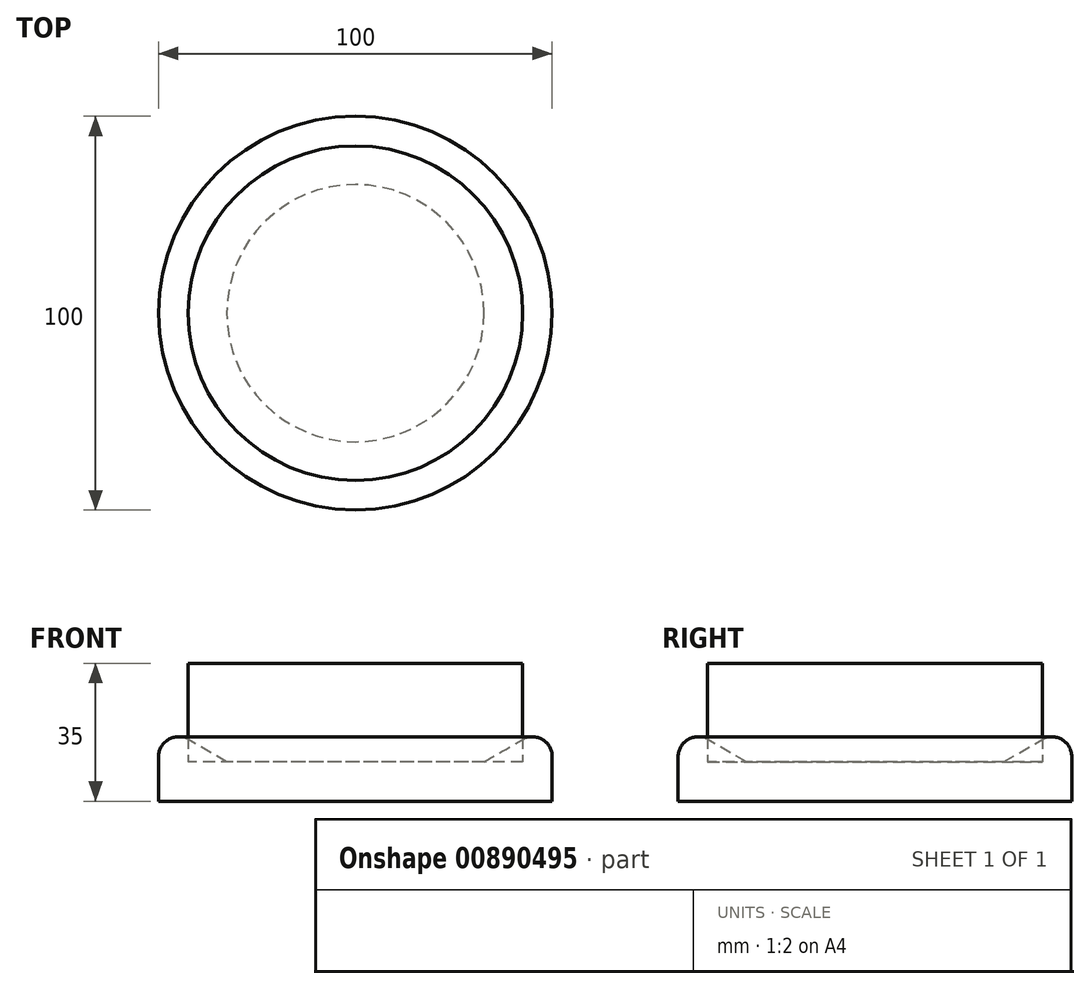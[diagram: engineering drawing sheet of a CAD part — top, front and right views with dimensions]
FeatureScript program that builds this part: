
annotation { "Feature Type Name" : "Feature", "Feature Type Description" : "" }
export const myFeature = defineFeature(function(context is Context, id is Id, definition is map)
    precondition{}
    {
        {
            var Q0;
            Q0=qCreatedBy(makeId("Front.planeOp"),FACE);
            var sketch = newSketch(context, id + "F0", { "sketchPlane" : qUnion([Q0])});
            skLineSegment(sketch, "E0", {"start": v(0, 0) * mm, "end": v(-50, 0) * mm});
            skLineSegment(sketch, "E1", {"start": v(-50, 0) * mm, "end": v(-50, 20) * mm});
            skLineSegment(sketch, "E2", {"start": v(-50, 20) * mm, "end": v(-32.68, 10) * mm});
            skLineSegment(sketch, "E3", {"start": v(-32.68, 10) * mm, "end": v(0, 10) * mm});
            skLineSegment(sketch, "E4", {"start": v(0, 10) * mm, "end": v(0, 0) * mm});
            skSolve(sketch);
        }
        {
            var Q0;
            Q0=makeQuery(id+"F0.imprint","IMPRINT",FACE,{"disambiguationData":[TD([[makeQuery(id+"F0.imprint","IMPRINT",EDGE,{"derivedFrom":sQuery(id+"F0.wireOp",EDGE,"E0")}),-1.0]])]});
            var Q1;
            Q1=sQuery(id+"F0.wireOp",EDGE,"E4");
            revolve(context, id + "F1", {"surfaceOperationType" : NewSurfaceOperationType.NEW, "entities" : qUnion([Q0]), "axis" : qUnion([Q1]), "revolveType" : RevolveType.FULL});
        }
        {
            var Q0;
            Q0=makeQuery(id+"F1.opRevolve","SWEPT_EDGE",EDGE,{"disambiguationData":[OSD([sQuery(id+"F0.wireOp",EDGE,"E1"),sQuery(id+"F0.wireOp",EDGE,"E2")])]});
            fillet(context, id + "F2", {"entities" : qUnion([Q0]), "radius" : 5 * mm, "tangentPropagation" : true, "allowEdgeOverflow" : false});
        }
        {
            var Q0;
            Q0=makeQuery(id+"F1.opRevolve","SWEPT_FACE",FACE,{"disambiguationData":[OSD([sQuery(id+"F0.wireOp",EDGE,"E3")])]});
            var sketch = newSketch(context, id + "F3", { "sketchPlane" : qUnion([Q0])});
            skCircle(sketch, "E5.0", {"center": v(0, 0) * mm, "radius": 32.68 * mm});
            skCircle(sketch, "E5.1", {"center": v(0, 0) * mm, "radius": 42.5 * mm});
            skSolve(sketch);
        }
        {
            var Q0;
            Q0=makeQuery(id+"F3.imprint","IMPRINT",FACE,{"disambiguationData":[TD([[makeQuery(id+"F3.imprint","IMPRINT",EDGE,{"derivedFrom":sQuery(id+"F3.wireOp",EDGE,"E5.0")}),-1.0]])]});
            var Q1;
            Q1=makeQuery(id+"F3.imprint","IMPRINT",FACE,{"disambiguationData":[TD([[makeQuery(id+"F3.imprint","IMPRINT",EDGE,{"derivedFrom":sQuery(id+"F3.wireOp",EDGE,"E5.0")}),1.0]])]});
            extrude(context, id + "F4", {"entities" : qUnion([Q0, Q1]), "depth" : 25 * mm, "offsetDistance" : 25 * mm});
        }
    });
